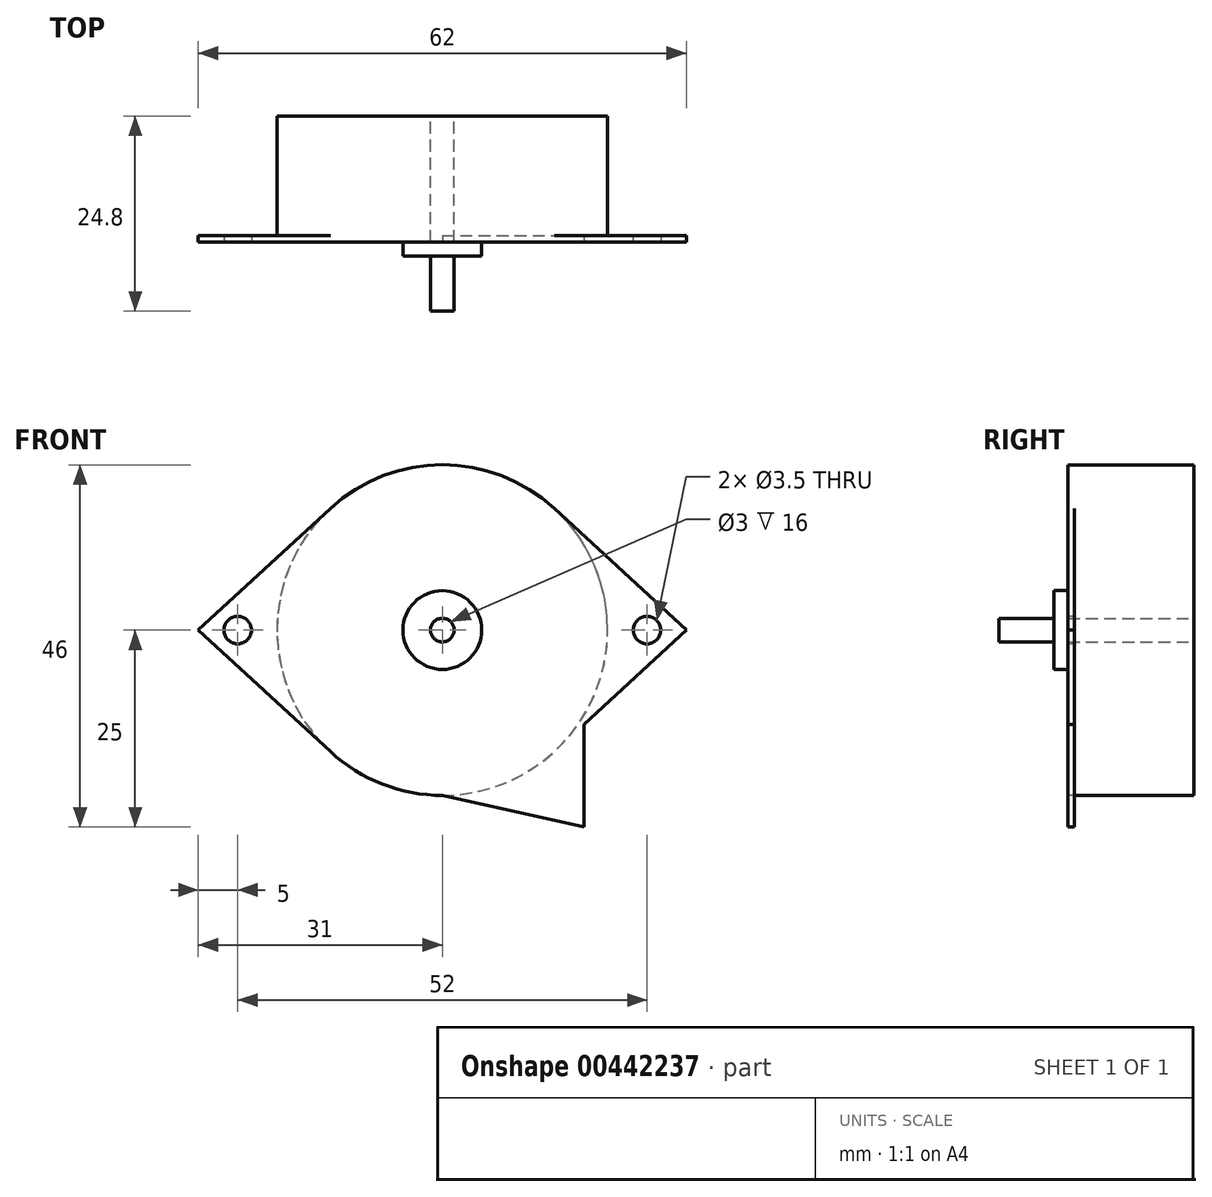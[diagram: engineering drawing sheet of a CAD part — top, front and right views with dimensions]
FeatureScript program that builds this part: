
annotation { "Feature Type Name" : "Feature", "Feature Type Description" : "" }
export const myFeature = defineFeature(function(context is Context, id is Id, definition is map)
    precondition{}
    {
        {
            var Q0;
            Q0=qCreatedBy(makeId("Front.planeOp"),FACE);
            var sketch = newSketch(context, id + "F0", { "sketchPlane" : qUnion([Q0])});
            skCircle(sketch, "E0", {"center": v(0, 0) * mm, "radius": 1.5 * mm});
            skCircle(sketch, "E1", {"center": v(0, 0) * mm, "radius": 21 * mm});
            skCircle(sketch, "E2", {"center": v(-26, 0) * mm, "radius": 1.75 * mm});
            skCircle(sketch, "E3", {"center": v(26, 0) * mm, "radius": 1.75 * mm});
            skLineSegment(sketch, "E4", {"start": v(-14.23, 15.45) * mm, "end": v(-31, 0) * mm});
            skLineSegment(sketch, "E5", {"start": v(-31, 0) * mm, "end": v(-14.23, -15.45) * mm});
            skLineSegment(sketch, "E6", {"start": v(18, -11.97) * mm, "end": v(31, 0) * mm});
            skLineSegment(sketch, "E7", {"start": v(31, 0) * mm, "end": v(14.23, 15.45) * mm});
            skCircle(sketch, "E8", {"center": v(0, 0) * mm, "radius": 5 * mm});
            skLineSegment(sketch, "E9", {"start": v(0, -21) * mm, "end": v(18, -25) * mm});
            skLineSegment(sketch, "E10", {"start": v(18, -25) * mm, "end": v(18, -11.97) * mm});
            skSolve(sketch);
        }
        {
            var Q0;
            Q0=makeQuery(id+"F0.imprint","IMPRINT",FACE,{"disambiguationData":[TD([[makeQuery(id+"F0.imprint","IMPRINT",EDGE,{"derivedFrom":sQuery(id+"F0.wireOp",EDGE,"E0")}),1.0]])]});
            var Q1;
            Q1=sQuery(id+"F0.wireOp",EDGE,"E0");
            extrude(context, id + "F1", {"entities" : qUnion([Q0]), "surfaceEntities" : qUnion([Q1]), "depth" : 8.8 * mm});
        }
        {
            var Q0;
            Q0=makeQuery(id+"F0.imprint","IMPRINT",FACE,{"disambiguationData":[TD([[makeQuery(id+"F0.imprint","IMPRINT",EDGE,{"derivedFrom":sQuery(id+"F0.wireOp",EDGE,"E0")}),-1.0]])]});
            var Q1;
            Q1=sQuery(id+"F0.wireOp",EDGE,"E8");
            extrude(context, id + "F2", {"entities" : qUnion([Q0]), "surfaceEntities" : qUnion([Q1]), "depth" : 1.8 * mm});
        }
        {
            var Q0;
            Q0=makeQuery(id+"F0.imprint","IMPRINT",FACE,{"disambiguationData":[TD([[makeQuery(id+"F0.imprint","IMPRINT",EDGE,{"derivedFrom":sQuery(id+"F0.wireOp",EDGE,"E8")}),-1.0]])]});
            var Q1;
            Q1=makeQuery(id+"F0.imprint","IMPRINT",FACE,{"disambiguationData":[TD([[makeQuery(id+"F0.imprint","IMPRINT",EDGE,{"derivedFrom":sQuery(id+"F0.wireOp",EDGE,"E0")}),-1.0]])]});
            extrude(context, id + "F3", {"entities" : qUnion([Q0, Q1]), "operationType" : NewBodyOperationType.ADD, "oppositeDirection" : true, "depth" : 16 * mm});
        }
        {
            var Q0;
            Q0=makeQuery(id+"F0.imprint","IMPRINT",FACE,{"disambiguationData":[TD([[makeQuery(id+"F0.imprint","IMPRINT",EDGE,{"derivedFrom":sQuery(id+"F0.wireOp",EDGE,"E2")}),-1.0]])]});
            var Q1;
            Q1=makeQuery(id+"F0.imprint","IMPRINT",FACE,{"disambiguationData":[TD([[makeQuery(id+"F0.imprint","IMPRINT",EDGE,{"derivedFrom":sQuery(id+"F0.wireOp",EDGE,"E3")}),-1.0]])]});
            var Q2;
            Q2=makeQuery(id+"F0.imprint","IMPRINT",FACE,{"disambiguationData":[TD([[makeQuery(id+"F0.imprint","IMPRINT",EDGE,{"derivedFrom":sQuery(id+"F0.wireOp",EDGE,"E8")}),-1.0]])]});
            extrude(context, id + "F4", {"entities" : qUnion([Q0, Q1, Q2]), "operationType" : NewBodyOperationType.ADD, "oppositeDirection" : true, "depth" : 0.8 * mm});
        }
    });
